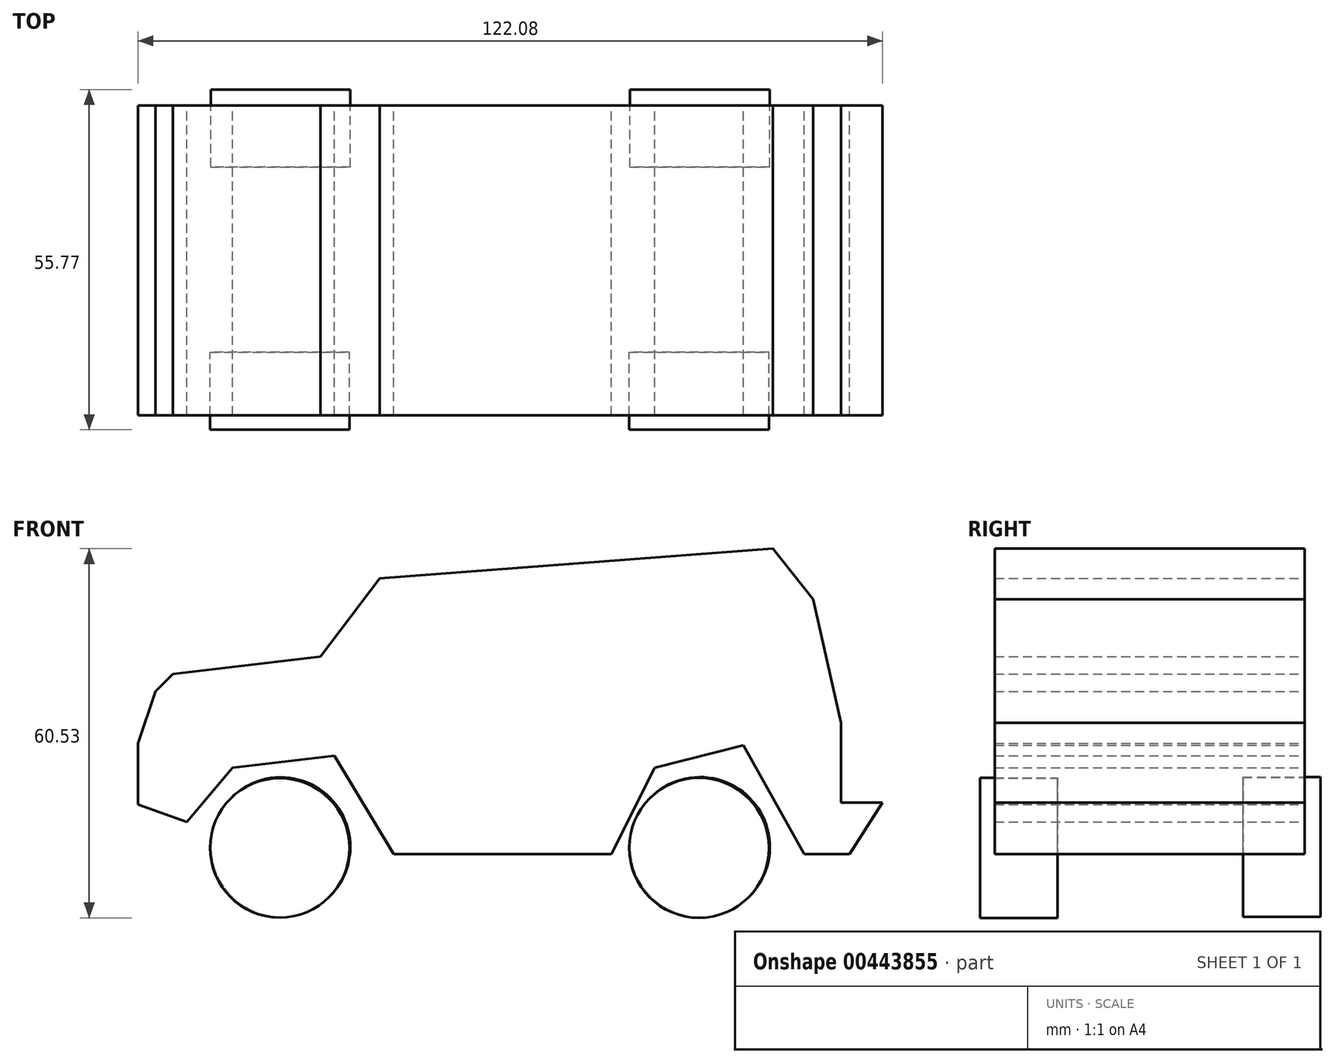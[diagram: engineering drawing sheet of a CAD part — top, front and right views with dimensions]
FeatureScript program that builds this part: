
annotation { "Feature Type Name" : "Feature", "Feature Type Description" : "" }
export const myFeature = defineFeature(function(context is Context, id is Id, definition is map)
    precondition{}
    {
        {
            var Q0;
            Q0=qCreatedBy(makeId("Front.planeOp"),FACE);
            var sketch = newSketch(context, id + "F0", { "sketchPlane" : qUnion([Q0])});
            skLineSegment(sketch, "E0", {"start": v(-56.2, 8.13) * mm, "end": v(-48.2, 5.28) * mm});
            skLineSegment(sketch, "E1", {"start": v(-56.2, 8.13) * mm, "end": v(-56.2, 18.11) * mm});
            skLineSegment(sketch, "E2", {"start": v(-56.2, 18.11) * mm, "end": v(-53.34, 26.67) * mm});
            skLineSegment(sketch, "E3", {"start": v(-53.34, 26.67) * mm, "end": v(-50.49, 29.52) * mm});
            skLineSegment(sketch, "E4", {"start": v(-50.49, 29.52) * mm, "end": v(-26.24, 32.37) * mm});
            skLineSegment(sketch, "E5", {"start": v(-26.24, 32.37) * mm, "end": v(-16.54, 45.21) * mm});
            skLineSegment(sketch, "E6", {"start": v(-16.54, 45.21) * mm, "end": v(47.92, 50.06) * mm});
            skLineSegment(sketch, "E7", {"start": v(47.92, 50.06) * mm, "end": v(54.48, 41.79) * mm});
            skLineSegment(sketch, "E8", {"start": v(54.48, 41.79) * mm, "end": v(59.04, 21.54) * mm});
            skLineSegment(sketch, "E9", {"start": v(59.04, 21.54) * mm, "end": v(59.04, 8.41) * mm});
            skLineSegment(sketch, "E10", {"start": v(59.04, 8.41) * mm, "end": v(65.9, 8.41) * mm});
            skLineSegment(sketch, "E11", {"start": v(65.9, 8.41) * mm, "end": v(60.47, 0) * mm});
            skLineSegment(sketch, "E12", {"start": v(60.47, 0) * mm, "end": v(53.05, 0) * mm});
            skLineSegment(sketch, "E13", {"start": v(53.05, 0) * mm, "end": v(43.07, 17.83) * mm});
            skLineSegment(sketch, "E14", {"start": v(43.07, 17.83) * mm, "end": v(28.52, 14.12) * mm});
            skLineSegment(sketch, "E15", {"start": v(28.52, 14.12) * mm, "end": v(21.4, 0) * mm});
            skLineSegment(sketch, "E16", {"start": v(21.4, 0) * mm, "end": v(-14.26, 0) * mm});
            skLineSegment(sketch, "E17", {"start": v(-14.26, 0) * mm, "end": v(-23.96, 16.12) * mm});
            skLineSegment(sketch, "E18", {"start": v(-23.96, 16.12) * mm, "end": v(-40.68, 14.15) * mm});
            skLineSegment(sketch, "E19", {"start": v(-40.68, 14.15) * mm, "end": v(-48.2, 5.28) * mm});
            skSolve(sketch);
        }
        {
            var Q0;
            Q0=makeQuery(id+"F0.imprint","IMPRINT",FACE,{"disambiguationData":[TD([[makeQuery(id+"F0.imprint","IMPRINT",EDGE,{"derivedFrom":sQuery(id+"F0.wireOp",EDGE,"E0")}),1.0]])]});
            extrude(context, id + "F1", {"entities" : qUnion([Q0]), "depth" : 50.8 * mm});
        }
        {
            var Q0;
            Q0=qCreatedBy(makeId("Front.planeOp"),FACE);
            var sketch = newSketch(context, id + "F2", { "sketchPlane" : qUnion([Q0])});
            skCircle(sketch, "E20", {"center": v(-32.8, 0) * mm, "radius": 11.43 * mm});
            skCircle(sketch, "E21", {"center": v(35.94, 0) * mm, "radius": 11.47 * mm});
            skCircle(sketch, "E22", {"center": v(-51.77, -37.5) * mm, "radius": 11.43 * mm});
            skCircle(sketch, "E23", {"center": v(16.97, -37.5) * mm, "radius": 11.47 * mm});
            skSolve(sketch);
        }
        {
            var Q0;
            Q0=qSketchRegion(id+"F2",true);
            extrude(context, id + "F3", {"entities" : qUnion([Q0]), "depth" : 12.7 * mm});
        }
        {
            var Q0;
            Q0=makeQuery(id+"F3.opExtrude","SWEPT_BODY",BODY,{"disambiguationData":[OSD([sQuery(id+"F2.wireOp",EDGE,"E22")])]});
            var Q1;
            Q1=makeQuery(id+"F3.opExtrude","SWEPT_BODY",BODY,{"disambiguationData":[OSD([sQuery(id+"F2.wireOp",EDGE,"E23")])]});
            transform(context, id + "F4", {"entities" : qUnion([Q0, Q1]), "transformType" : TransformType.TRANSLATION_3D, "dx" : 18.83 * mm, "dy" : -40.5 * mm, "dz" : 38.5 * mm, "makeCopy" : false});
        }
        {
            var Q0;
            Q0=makeQuery(id+"F3.opExtrude","SWEPT_BODY",BODY,{"disambiguationData":[OSD([sQuery(id+"F2.wireOp",EDGE,"E21")])]});
            var Q1;
            Q1=makeQuery(id+"F3.opExtrude","SWEPT_BODY",BODY,{"disambiguationData":[OSD([sQuery(id+"F2.wireOp",EDGE,"E20")])]});
            transform(context, id + "F5", {"entities" : qUnion([Q0, Q1]), "transformType" : TransformType.TRANSLATION_3D, "dx" : 0 * mm, "dy" : 2.57 * mm, "dz" : 1.14 * mm, "makeCopy" : false});
        }
    });
